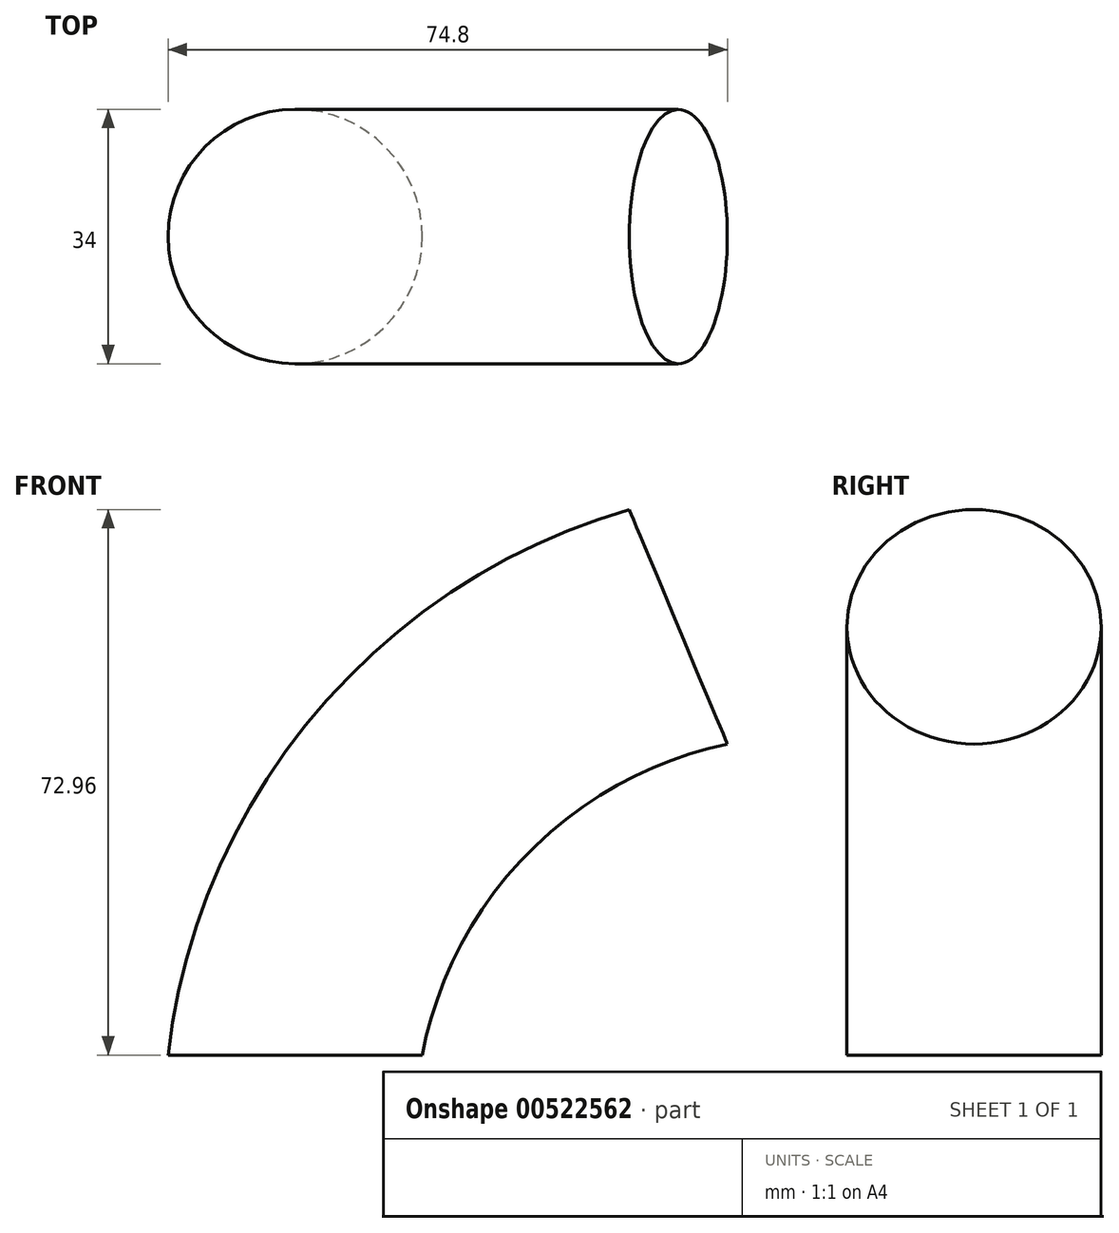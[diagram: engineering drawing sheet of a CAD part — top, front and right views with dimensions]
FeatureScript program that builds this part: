
annotation { "Feature Type Name" : "Feature", "Feature Type Description" : "" }
export const myFeature = defineFeature(function(context is Context, id is Id, definition is map)
    precondition{}
    {
        {
            var Q0;
            Q0=qCreatedBy(makeId("Front.planeOp"),FACE);
            var sketch = newSketch(context, id + "F0", { "sketchPlane" : qUnion([Q0])});
            skArc(sketch, "E0", {"start": v(51.23, 57.27) * mm, "mid": v(16.96, 36.38) * mm, "end": v(0, 0) * mm});
            skSolve(sketch);
        }
        {
            var Q0;
            Q0=qCreatedBy(makeId("Top.planeOp"),FACE);
            var sketch = newSketch(context, id + "F1", { "sketchPlane" : qUnion([Q0])});
            skCircle(sketch, "E1", {"center": v(0, 0) * mm, "radius": 17 * mm});
            skSolve(sketch);
        }
        {
            var Q0;
            Q0=makeQuery(id+"F1.imprint","IMPRINT",FACE,{"disambiguationData":[TD([[makeQuery(id+"F1.imprint","IMPRINT",EDGE,{"derivedFrom":sQuery(id+"F1.wireOp",EDGE,"E1")}),1.0]])]});
            var Q1;
            Q1=sQuery(id+"F0.wireOp",EDGE,"E0");
            sweep(context, id + "F2", {"profiles" : qUnion([Q0]), "path" : qUnion([Q1])});
        }
    });
